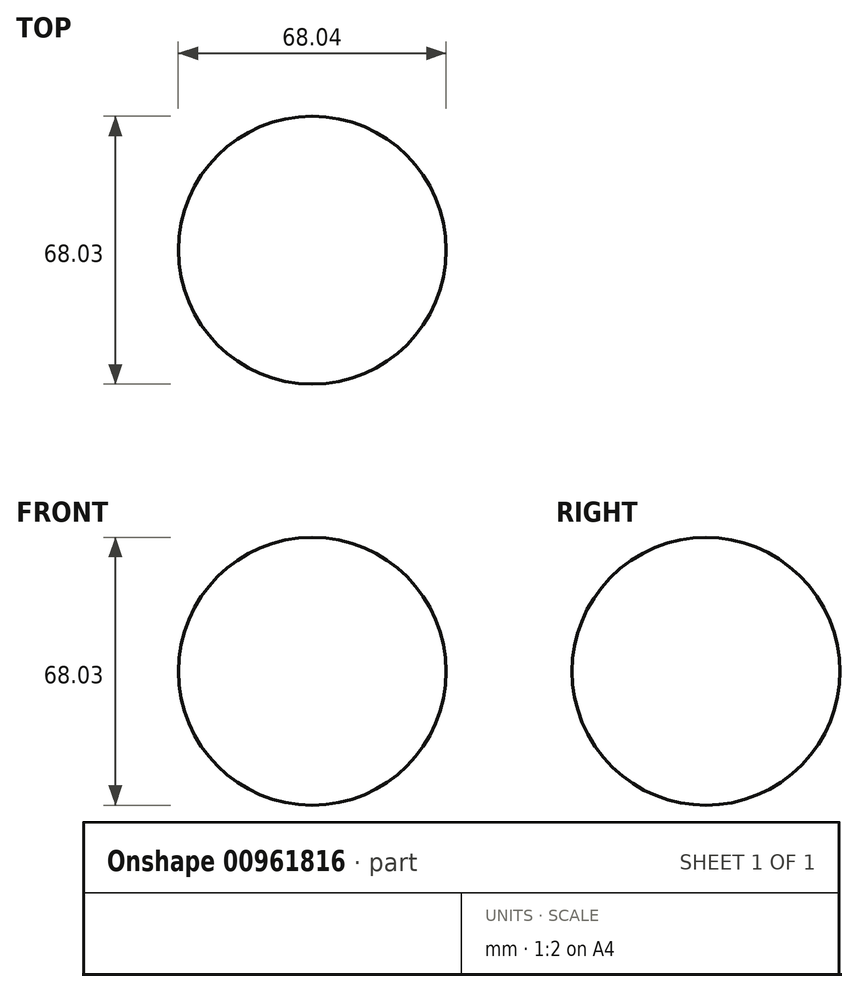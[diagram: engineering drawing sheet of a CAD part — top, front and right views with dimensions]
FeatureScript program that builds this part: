
annotation { "Feature Type Name" : "Feature", "Feature Type Description" : "" }
export const myFeature = defineFeature(function(context is Context, id is Id, definition is map)
    precondition{}
    {
        {
            var Q0;
            Q0=qCreatedBy(makeId("Right.planeOp"),FACE);
            var sketch = newSketch(context, id + "F0", { "sketchPlane" : qUnion([Q0])});
            skArc(sketch, "E0", {"start": v(-56.36, 0) * mm, "mid": v(-9.13, -9.13) * mm, "end": v(0, 38.1) * mm});
            skLineSegment(sketch, "E1", {"start": v(-56.36, 0) * mm, "end": v(0, 38.1) * mm});
            skSolve(sketch);
        }
        {
            var Q0;
            Q0=makeQuery(id+"F0.imprint","IMPRINT",FACE,{"disambiguationData":[TD([[makeQuery(id+"F0.imprint","IMPRINT",EDGE,{"derivedFrom":sQuery(id+"F0.wireOp",EDGE,"E0")}),1.0]])]});
            var Q1;
            Q1=sQuery(id+"F0.wireOp",EDGE,"E1");
            revolve(context, id + "F1", {"surfaceOperationType" : NewSurfaceOperationType.NEW, "entities" : qUnion([Q0]), "axis" : qUnion([Q1]), "revolveType" : RevolveType.FULL});
        }
    });
